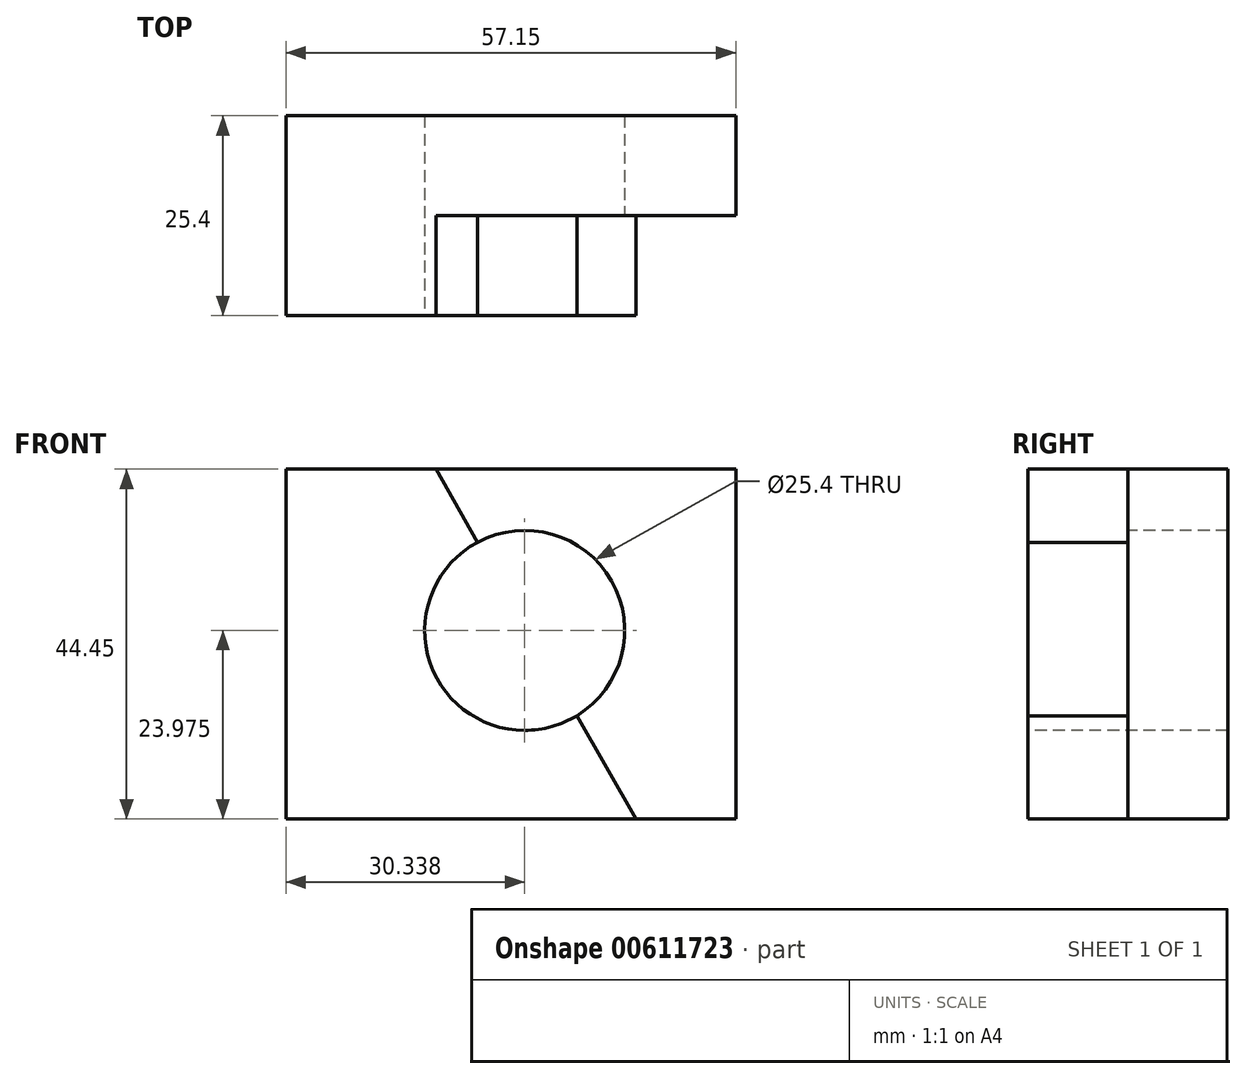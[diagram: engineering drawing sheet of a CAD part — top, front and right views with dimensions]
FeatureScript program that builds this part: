
annotation { "Feature Type Name" : "Feature", "Feature Type Description" : "" }
export const myFeature = defineFeature(function(context is Context, id is Id, definition is map)
    precondition{}
    {
        {
            var Q0;
            Q0=qCreatedBy(makeId("Front.planeOp"),FACE);
            var sketch = newSketch(context, id + "F0", { "sketchPlane" : qUnion([Q0])});
            skLineSegment(sketch, "E0.bottom", {"start": v(0, 0) * mm, "end": v(-57.15, 0) * mm});
            skLineSegment(sketch, "E0.top", {"start": v(0, 44.45) * mm, "end": v(-57.15, 44.45) * mm});
            skLineSegment(sketch, "E0.left", {"start": v(0, 0) * mm, "end": v(0, 44.45) * mm});
            skLineSegment(sketch, "E0.right", {"start": v(-57.15, 0) * mm, "end": v(-57.15, 44.45) * mm});
            skSolve(sketch);
        }
        {
            var Q0;
            Q0=makeQuery(id+"F0.imprint","IMPRINT",FACE,{"disambiguationData":[TD([[makeQuery(id+"F0.imprint","IMPRINT",EDGE,{"derivedFrom":sQuery(id+"F0.wireOp",EDGE,"E0.bottom")}),-1.0]])]});
            extrude(context, id + "F1", {"entities" : qUnion([Q0]), "depth" : 25.4 * mm, "offsetDistance" : 25.4 * mm});
        }
        {
            var Q0;
            Q0=makeQuery(id+"F1.opExtrude","CAP_FACE",FACE,{"disambiguationData":[OSD([sQuery(id+"F0.wireOp",EDGE,"E0.bottom"),sQuery(id+"F0.wireOp",EDGE,"E0.top"),sQuery(id+"F0.wireOp",EDGE,"E0.left"),sQuery(id+"F0.wireOp",EDGE,"E0.right")])],"isStart":false});
            var sketch = newSketch(context, id + "F2", { "sketchPlane" : qUnion([Q0])});
            skLineSegment(sketch, "E1", {"start": v(-57.15, 44.45) * mm, "end": v(-38.1, 44.45) * mm});
            skLineSegment(sketch, "E2", {"start": v(0, 0) * mm, "end": v(-12.7, 0) * mm});
            skLineSegment(sketch, "E3", {"start": v(-38.1, 44.45) * mm, "end": v(-12.7, 0) * mm});
            skSolve(sketch);
        }
        {
            var Q0;
            Q0=makeQuery(id+"F2.imprint","IMPRINT",FACE,{"disambiguationData":[TD([[makeQuery(id+"F2.imprint","IMPRINT",EDGE,{"derivedFrom":sQuery(id+"F2.wireOp",EDGE,"E1")}),1.0]])]});
            var sketch = newSketch(context, id + "F3", { "sketchPlane" : qUnion([Q0])});
            skCircle(sketch, "E4", {"center": v(-26.81, 23.97) * mm, "radius": 12.7 * mm});
            skSolve(sketch);
        }
        {
            var Q0;
            Q0 = qSketchRegion(id + "F3", true);
            extrude(context, id + "F4", {"entities" : qUnion([Q0]), "operationType" : NewBodyOperationType.REMOVE, "endBound" : BoundingType.THROUGH_ALL, "oppositeDirection" : true, "depth" : 25.4 * mm, "offsetDistance" : 25.4 * mm});
        }
        {
            var Q0;
            Q0=makeQuery(id+"F2.imprint","IMPRINT",FACE,{"disambiguationData":[TD([[makeQuery(id+"F2.imprint","IMPRINT",EDGE,{"derivedFrom":sQuery(id+"F2.wireOp",EDGE,"E2")}),-1.0]])]});
            extrude(context, id + "F5", {"entities" : qUnion([Q0]), "operationType" : NewBodyOperationType.REMOVE, "oppositeDirection" : true, "depth" : 12.7 * mm, "offsetDistance" : 25.4 * mm});
        }
    });
